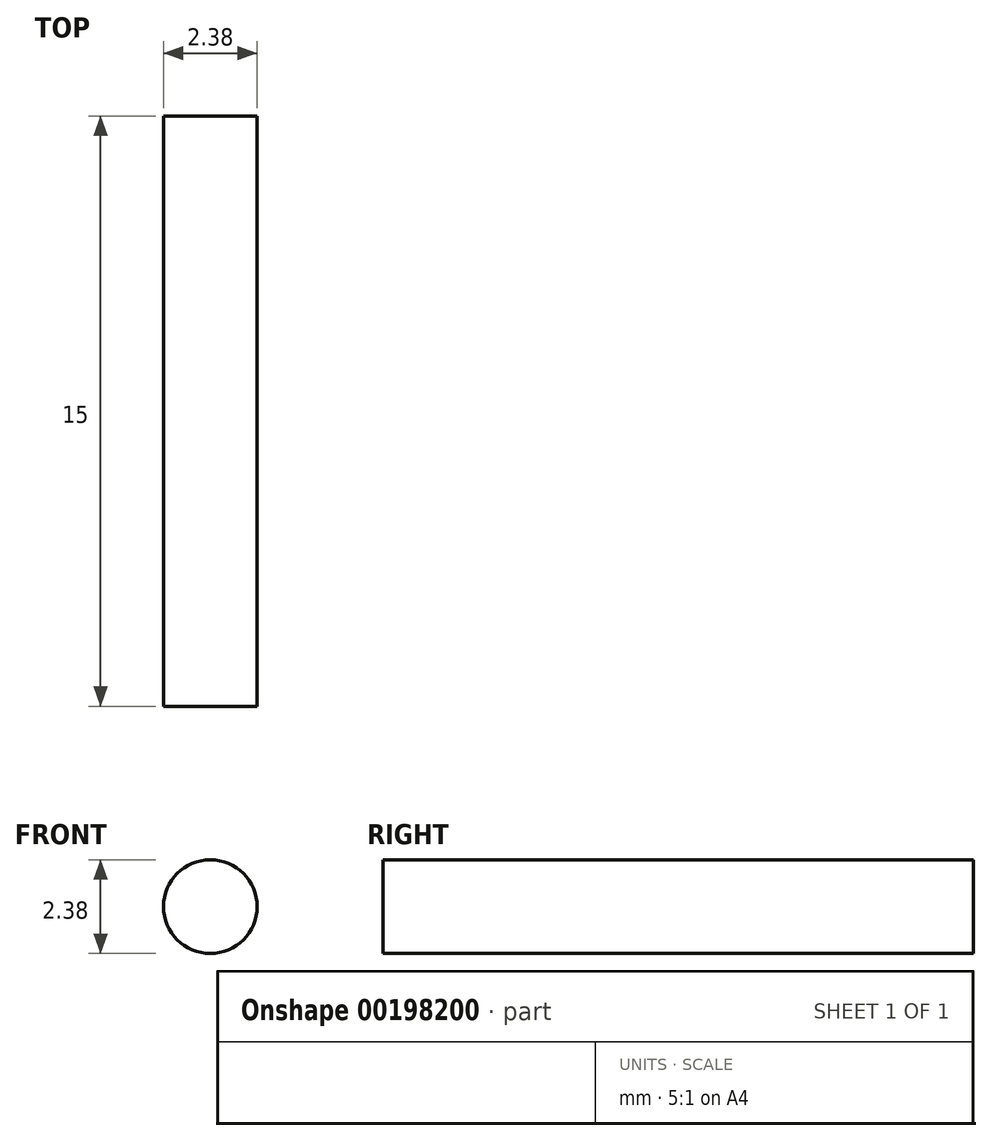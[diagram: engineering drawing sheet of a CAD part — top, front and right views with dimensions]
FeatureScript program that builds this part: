
annotation { "Feature Type Name" : "Feature", "Feature Type Description" : "" }
export const myFeature = defineFeature(function(context is Context, id is Id, definition is map)
    precondition{}
    {
        {
            var Q0;
            Q0=qCreatedBy(makeId("Front.planeOp"),FACE);
            var sketch = newSketch(context, id + "F0", { "sketchPlane" : qUnion([Q0])});
            skCircle(sketch, "E0", {"center": v(0, 0) * mm, "radius": 1.2 * mm});
            skSolve(sketch);
        }
        {
            var Q0;
            Q0=qSketchRegion(id+"F0",true);
            extrude(context, id + "F1", {"entities" : qUnion([Q0]), "depth" : 15 * mm});
        }
    });
